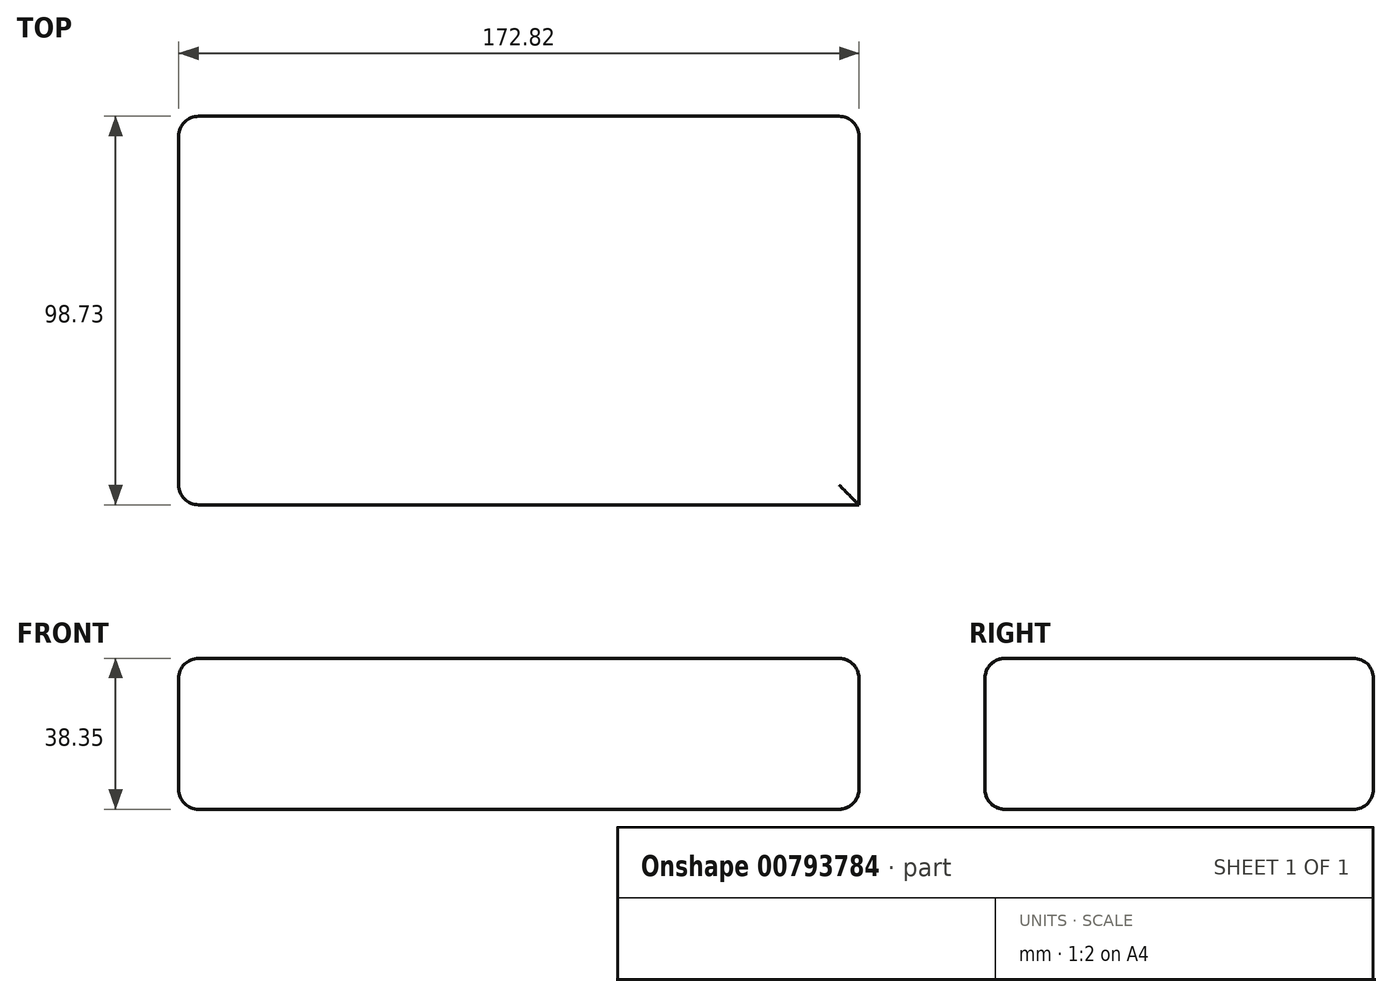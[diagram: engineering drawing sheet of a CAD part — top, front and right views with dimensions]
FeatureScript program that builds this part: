
annotation { "Feature Type Name" : "Feature", "Feature Type Description" : "" }
export const myFeature = defineFeature(function(context is Context, id is Id, definition is map)
    precondition{}
    {
        {
            var Q0;
            Q0=qCreatedBy(makeId("Top.planeOp"),FACE);
            var sketch = newSketch(context, id + "F0", { "sketchPlane" : qUnion([Q0])});
            skLineSegment(sketch, "E0.bottom", {"start": v(-86.79, 52.23) * mm, "end": v(86.03, 52.23) * mm});
            skLineSegment(sketch, "E0.top", {"start": v(-86.79, -46.5) * mm, "end": v(86.03, -46.5) * mm});
            skLineSegment(sketch, "E0.left", {"start": v(-86.79, 52.23) * mm, "end": v(-86.79, -46.5) * mm});
            skLineSegment(sketch, "E0.right", {"start": v(86.03, 52.23) * mm, "end": v(86.03, -46.5) * mm});
            skSolve(sketch);
        }
        {
            var Q0;
            Q0 = qSketchRegion(id + "F0", true);
            extrude(context, id + "F1", {"entities" : qUnion([Q0]), "depth" : 38.35 * mm, "offsetDistance" : 25.4 * mm});
        }
        {
            var Q0;
            Q0=makeQuery(id+"F1.opExtrude","CAP_EDGE",EDGE,{"disambiguationData":[OSD([sQuery(id+"F0.wireOp",EDGE,"E0.top")])],"isStart":false});
            var Q1;
            Q1=makeQuery(id+"F1.opExtrude","CAP_EDGE",EDGE,{"disambiguationData":[OSD([sQuery(id+"F0.wireOp",EDGE,"E0.top")])],"isStart":true});
            var Q2;
            Q2=makeQuery(id+"F1.opExtrude","CAP_EDGE",EDGE,{"disambiguationData":[OSD([sQuery(id+"F0.wireOp",EDGE,"E0.right")])],"isStart":false});
            var Q3;
            Q3=makeQuery(id+"F1.opExtrude","CAP_EDGE",EDGE,{"disambiguationData":[OSD([sQuery(id+"F0.wireOp",EDGE,"E0.right")])],"isStart":true});
            var Q4;
            Q4=makeQuery(id+"F1.opExtrude","CAP_EDGE",EDGE,{"disambiguationData":[OSD([sQuery(id+"F0.wireOp",EDGE,"E0.bottom")])],"isStart":false});
            var Q5;
            Q5=makeQuery(id+"F1.opExtrude","CAP_EDGE",EDGE,{"disambiguationData":[OSD([sQuery(id+"F0.wireOp",EDGE,"E0.bottom")])],"isStart":true});
            var Q6;
            Q6=makeQuery(id+"F1.opExtrude","SWEPT_EDGE",EDGE,{"disambiguationData":[OSD([sQuery(id+"F0.wireOp",EDGE,"E0.bottom"),sQuery(id+"F0.wireOp",EDGE,"E0.right")])]});
            var Q7;
            Q7=makeQuery(id+"F1.opExtrude","SWEPT_EDGE",EDGE,{"disambiguationData":[OSD([sQuery(id+"F0.wireOp",EDGE,"E0.bottom"),sQuery(id+"F0.wireOp",EDGE,"E0.left")])]});
            var Q8;
            Q8=makeQuery(id+"F1.opExtrude","CAP_EDGE",EDGE,{"disambiguationData":[OSD([sQuery(id+"F0.wireOp",EDGE,"E0.left")])],"isStart":false});
            var Q9;
            Q9=makeQuery(id+"F1.opExtrude","CAP_EDGE",EDGE,{"disambiguationData":[OSD([sQuery(id+"F0.wireOp",EDGE,"E0.left")])],"isStart":true});
            var Q10;
            Q10=makeQuery(id+"F1.opExtrude","SWEPT_EDGE",EDGE,{"disambiguationData":[OSD([sQuery(id+"F0.wireOp",EDGE,"E0.top"),sQuery(id+"F0.wireOp",EDGE,"E0.left")])]});
            fillet(context, id + "F2", {"entities" : qUnion([Q0, Q1, Q2, Q3, Q4, Q5, Q6, Q7, Q8, Q9, Q10]), "radius" : 5.08 * mm, "tangentPropagation" : true, "allowEdgeOverflow" : false});
        }
    });
